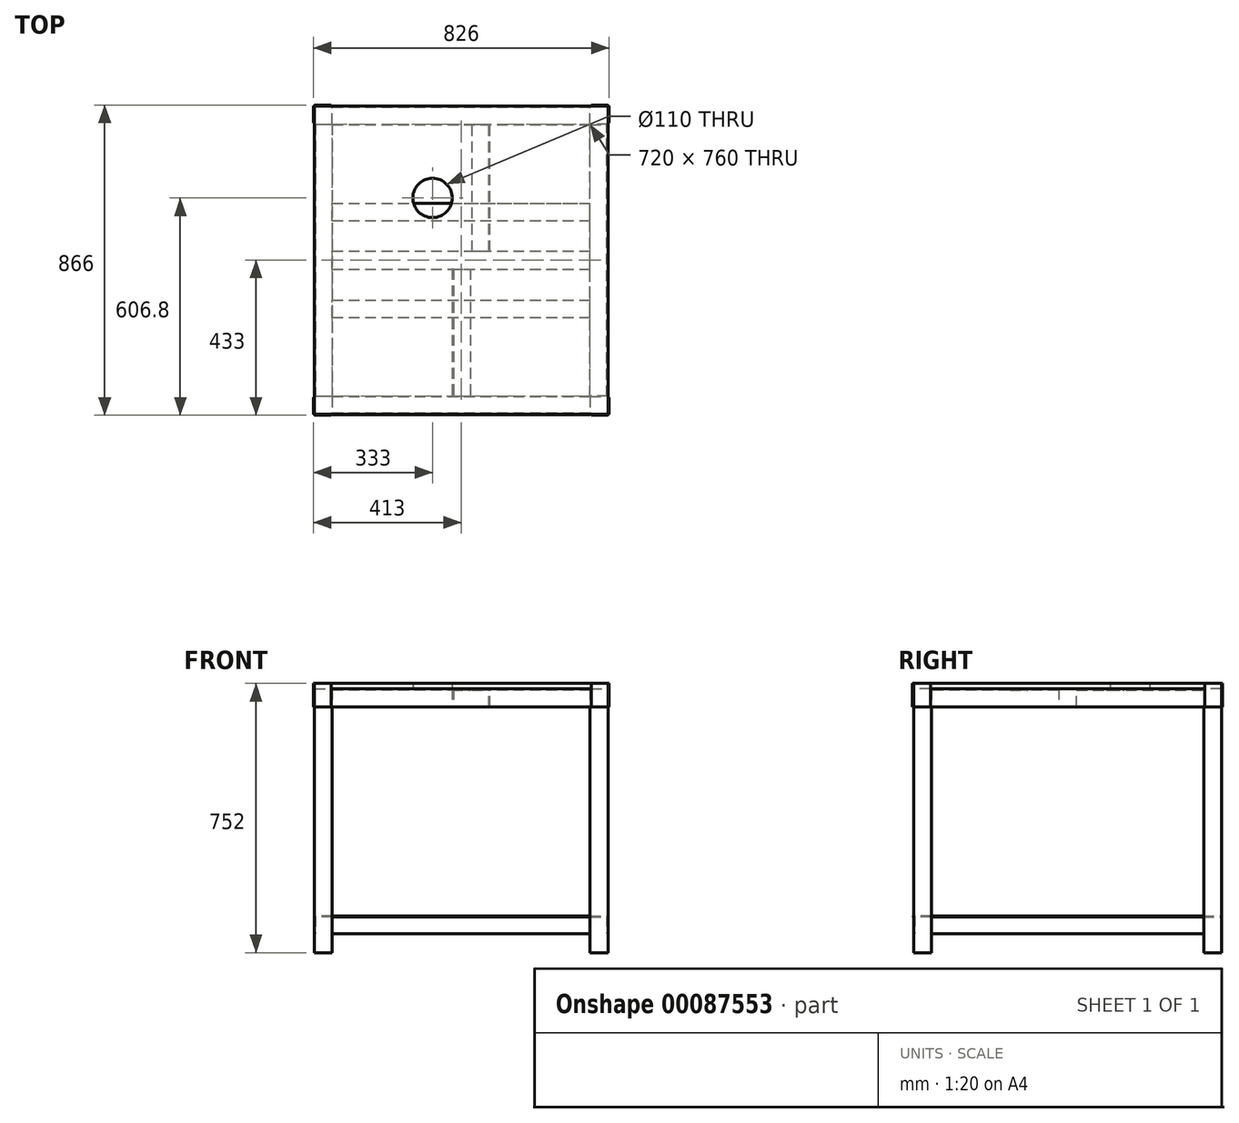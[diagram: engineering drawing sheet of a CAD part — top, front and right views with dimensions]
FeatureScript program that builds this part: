
annotation { "Feature Type Name" : "Feature", "Feature Type Description" : "" }
export const myFeature = defineFeature(function(context is Context, id is Id, definition is map)
    precondition{}
    {
        {
            var Q0;
            Q0=qCreatedBy(makeId("Top.planeOp"),FACE);
            var sketch = newSketch(context, id + "F0", { "sketchPlane" : qUnion([Q0])});
            skLineSegment(sketch, "E0", {"start": v(-475, -20) * mm, "end": v(-475, 410) * mm});
            skLineSegment(sketch, "E1", {"start": v(-475, -20) * mm, "end": v(-475, -450) * mm});
            skLineSegment(sketch, "E2", {"start": v(345, -20) * mm, "end": v(345, -450) * mm});
            skLineSegment(sketch, "E3", {"start": v(345, -20) * mm, "end": v(345, 410) * mm});
            skLineSegment(sketch, "E4", {"start": v(-425, -20) * mm, "end": v(-425, 360) * mm});
            skLineSegment(sketch, "E5", {"start": v(-425, -20) * mm, "end": v(-425, -400) * mm});
            skLineSegment(sketch, "E6", {"start": v(295, -20) * mm, "end": v(295, -400) * mm});
            skLineSegment(sketch, "E7", {"start": v(295, -20) * mm, "end": v(295, 360) * mm});
            skLineSegment(sketch, "E8", {"start": v(-425, 360) * mm, "end": v(295, 360) * mm});
            skLineSegment(sketch, "E9", {"start": v(-475, -450) * mm, "end": v(345, -450) * mm});
            skLineSegment(sketch, "E10", {"start": v(-425, -400) * mm, "end": v(295, -400) * mm});
            skLineSegment(sketch, "E11", {"start": v(-475, 410) * mm, "end": v(345, 410) * mm});
            skSolve(sketch);
        }
        {
            var Q0;
            Q0=makeQuery(id+"F0.imprint","IMPRINT",FACE,{"disambiguationData":[TD([[makeQuery(id+"F0.imprint","IMPRINT",EDGE,{"derivedFrom":sQuery(id+"F0.wireOp",EDGE,"E0")}),-1.0]])]});
            extrude(context, id + "F1", {"entities" : qUnion([Q0]), "depth" : 50 * mm});
        }
        {
            var Q0;
            Q0=makeQuery(id+"F1.opExtrude","SWEPT_BODY",BODY,{"disambiguationData":[OSD([sQuery(id+"F0.wireOp",EDGE,"E0"),sQuery(id+"F0.wireOp",EDGE,"E1"),sQuery(id+"F0.wireOp",EDGE,"E2"),sQuery(id+"F0.wireOp",EDGE,"E3"),sQuery(id+"F0.wireOp",EDGE,"E4"),sQuery(id+"F0.wireOp",EDGE,"E5"),sQuery(id+"F0.wireOp",EDGE,"E6"),sQuery(id+"F0.wireOp",EDGE,"E7"),sQuery(id+"F0.wireOp",EDGE,"E8"),sQuery(id+"F0.wireOp",EDGE,"E9"),sQuery(id+"F0.wireOp",EDGE,"E10"),sQuery(id+"F0.wireOp",EDGE,"E11")])]});
            transform(context, id + "F2", {"entities" : qUnion([Q0]), "transformType" : TransformType.TRANSLATION_3D, "dx" : 65 * mm, "dy" : 20 * mm, "dz" : 0 * mm, "makeCopy" : false});
        }
        {
            var Q0;
            Q0=makeQuery(id+"F1.opExtrude","SWEPT_BODY",BODY,{"disambiguationData":[OSD([sQuery(id+"F0.wireOp",EDGE,"E0"),sQuery(id+"F0.wireOp",EDGE,"E1"),sQuery(id+"F0.wireOp",EDGE,"E2"),sQuery(id+"F0.wireOp",EDGE,"E3"),sQuery(id+"F0.wireOp",EDGE,"E4"),sQuery(id+"F0.wireOp",EDGE,"E5"),sQuery(id+"F0.wireOp",EDGE,"E6"),sQuery(id+"F0.wireOp",EDGE,"E7"),sQuery(id+"F0.wireOp",EDGE,"E8"),sQuery(id+"F0.wireOp",EDGE,"E9"),sQuery(id+"F0.wireOp",EDGE,"E10"),sQuery(id+"F0.wireOp",EDGE,"E11")])]});
            transform(context, id + "F3", {"entities" : qUnion([Q0]), "transformType" : TransformType.TRANSLATION_3D, "dx" : 0 * mm, "dy" : 0 * mm, "dz" : -162 * mm, "makeCopy" : false});
        }
        {
            var Q0;
            Q0=qCreatedBy(makeId("Top.planeOp"),FACE);
            var sketch = newSketch(context, id + "F4", { "sketchPlane" : qUnion([Q0])});
            skLineSegment(sketch, "E12", {"start": v(-450, -20) * mm, "end": v(-450, 410) * mm});
            skLineSegment(sketch, "E13", {"start": v(370, -20) * mm, "end": v(370, -450) * mm});
            skLineSegment(sketch, "E14.bottom", {"start": v(-450, 410) * mm, "end": v(370, 410) * mm});
            skLineSegment(sketch, "E14.top", {"start": v(-450, -450) * mm, "end": v(370, -450) * mm});
            skLineSegment(sketch, "E14.left", {"start": v(-450, 410) * mm, "end": v(-450, -450) * mm});
            skLineSegment(sketch, "E14.right", {"start": v(370, 410) * mm, "end": v(370, -450) * mm});
            skSolve(sketch);
        }
        {
            var Q0;
            {var subQ0=sQuery(id+"F4.wireOp",EDGE,"E14.bottom");Q0=makeQuery(id+"F4.imprint","IMPRINT",FACE,{"disambiguationData":[TD([[makeQuery(id+"F4.imprint","IMPRINT",EDGE,{"derivedFrom":subQ0}),-1.0]])]});}
            extrude(context, id + "F5", {"entities" : qUnion([Q0]), "depth" : 15 * mm});
        }
        {
            var Q0;
            Q0=makeQuery(id+"F5.opExtrude","SWEPT_BODY",BODY,{"disambiguationData":[OSD([sQuery(id+"F4.wireOp",EDGE,"E14.bottom"),sQuery(id+"F4.wireOp",EDGE,"E14.top"),sQuery(id+"F4.wireOp",EDGE,"E14.left"),sQuery(id+"F4.wireOp",EDGE,"E14.right")])]});
            transform(context, id + "F6", {"entities" : qUnion([Q0]), "transformType" : TransformType.TRANSLATION_3D, "dx" : 0 * mm, "dy" : 0 * mm, "dz" : -112 * mm, "makeCopy" : false});
        }
        {
            var Q0;
            Q0=qCreatedBy(makeId("Top.planeOp"),FACE);
            var sketch = newSketch(context, id + "F7", { "sketchPlane" : qUnion([Q0])});
            skLineSegment(sketch, "E15", {"start": v(0, 0) * mm, "end": v(-410, 0) * mm});
            skLineSegment(sketch, "E16", {"start": v(0, 0) * mm, "end": v(410, 0) * mm});
            skLineSegment(sketch, "E17", {"start": v(-410, 0) * mm, "end": v(-410, 380) * mm});
            skLineSegment(sketch, "E18", {"start": v(410, 0) * mm, "end": v(410, 380) * mm});
            skLineSegment(sketch, "E19", {"start": v(-410, 0) * mm, "end": v(-410, -380) * mm});
            skLineSegment(sketch, "E20", {"start": v(410, 0) * mm, "end": v(410, -380) * mm});
            skLineSegment(sketch, "E21.bottom", {"start": v(-410, 380) * mm, "end": v(-360, 380) * mm});
            skLineSegment(sketch, "E21.top", {"start": v(-410, 430) * mm, "end": v(-360, 430) * mm});
            skLineSegment(sketch, "E21.left", {"start": v(-410, 380) * mm, "end": v(-410, 430) * mm});
            skLineSegment(sketch, "E21.right", {"start": v(-360, 380) * mm, "end": v(-360, 430) * mm});
            skLineSegment(sketch, "E22.bottom", {"start": v(-410, -380) * mm, "end": v(-360, -380) * mm});
            skLineSegment(sketch, "E22.top", {"start": v(-410, -430) * mm, "end": v(-360, -430) * mm});
            skLineSegment(sketch, "E22.left", {"start": v(-410, -380) * mm, "end": v(-410, -430) * mm});
            skLineSegment(sketch, "E22.right", {"start": v(-360, -380) * mm, "end": v(-360, -430) * mm});
            skLineSegment(sketch, "E23.bottom", {"start": v(410, -380) * mm, "end": v(360, -380) * mm});
            skLineSegment(sketch, "E23.top", {"start": v(410, -430) * mm, "end": v(360, -430) * mm});
            skLineSegment(sketch, "E23.left", {"start": v(410, -380) * mm, "end": v(410, -430) * mm});
            skLineSegment(sketch, "E23.right", {"start": v(360, -380) * mm, "end": v(360, -430) * mm});
            skLineSegment(sketch, "E24.bottom", {"start": v(410, 380) * mm, "end": v(360, 380) * mm});
            skLineSegment(sketch, "E24.top", {"start": v(410, 430) * mm, "end": v(360, 430) * mm});
            skLineSegment(sketch, "E24.left", {"start": v(410, 380) * mm, "end": v(410, 430) * mm});
            skLineSegment(sketch, "E24.right", {"start": v(360, 380) * mm, "end": v(360, 430) * mm});
            skLineSegment(sketch, "E25", {"start": v(-410, 0) * mm, "end": v(-410, -430) * mm});
            skLineSegment(sketch, "E26", {"start": v(-410, 0) * mm, "end": v(-410, 430) * mm});
            skSolve(sketch);
        }
        {
            var Q0;
            Q0 = qSketchRegion(id + "F7", true);
            extrude(context, id + "F8", {"entities" : qUnion([Q0]), "depth" : 687 * mm});
        }
        {
            var Q0;
            Q0=makeQuery(id+"F8.opExtrude","SWEPT_BODY",BODY,{"disambiguationData":[OSD([sQuery(id+"F7.wireOp",EDGE,"E21.bottom"),sQuery(id+"F7.wireOp",EDGE,"E21.top"),sQuery(id+"F7.wireOp",EDGE,"E21.left"),sQuery(id+"F7.wireOp",EDGE,"E21.right")])]});
            var Q1;
            Q1=makeQuery(id+"F8.opExtrude","SWEPT_BODY",BODY,{"disambiguationData":[OSD([sQuery(id+"F7.wireOp",EDGE,"E22.bottom"),sQuery(id+"F7.wireOp",EDGE,"E22.top"),sQuery(id+"F7.wireOp",EDGE,"E22.left"),sQuery(id+"F7.wireOp",EDGE,"E22.right")])]});
            var Q2;
            Q2=makeQuery(id+"F8.opExtrude","SWEPT_BODY",BODY,{"disambiguationData":[OSD([sQuery(id+"F7.wireOp",EDGE,"E23.bottom"),sQuery(id+"F7.wireOp",EDGE,"E23.top"),sQuery(id+"F7.wireOp",EDGE,"E23.left"),sQuery(id+"F7.wireOp",EDGE,"E23.right")])]});
            var Q3;
            Q3=makeQuery(id+"F8.opExtrude","SWEPT_BODY",BODY,{"disambiguationData":[OSD([sQuery(id+"F7.wireOp",EDGE,"E24.bottom"),sQuery(id+"F7.wireOp",EDGE,"E24.top"),sQuery(id+"F7.wireOp",EDGE,"E24.left"),sQuery(id+"F7.wireOp",EDGE,"E24.right")])]});
            transform(context, id + "F9", {"entities" : qUnion([Q0, Q1, Q2, Q3]), "transformType" : TransformType.TRANSLATION_3D, "dx" : 0 * mm, "dy" : 0 * mm, "dz" : -849 * mm, "makeCopy" : false});
        }
        {
            var Q0;
            Q0=qCreatedBy(makeId("Top.planeOp"),FACE);
            var sketch = newSketch(context, id + "F10", { "sketchPlane" : qUnion([Q0])});
            skLineSegment(sketch, "E27", {"start": v(0, 0) * mm, "end": v(-410, 0) * mm});
            skLineSegment(sketch, "E28", {"start": v(0, 0) * mm, "end": v(410, 0) * mm});
            skLineSegment(sketch, "E29", {"start": v(-410, 0) * mm, "end": v(-410, -383) * mm});
            skLineSegment(sketch, "E30", {"start": v(410, 0) * mm, "end": v(410, -383) * mm});
            skLineSegment(sketch, "E31", {"start": v(-410, 0) * mm, "end": v(-410, 383) * mm});
            skLineSegment(sketch, "E32", {"start": v(410, 0) * mm, "end": v(410, 383) * mm});
            skLineSegment(sketch, "E33.bottom", {"start": v(-410, 383) * mm, "end": v(-413, 383) * mm});
            skLineSegment(sketch, "E33.top", {"start": v(-410, 433) * mm, "end": v(-413, 433) * mm});
            skLineSegment(sketch, "E33.left", {"start": v(-410, 383) * mm, "end": v(-410, 433) * mm});
            skLineSegment(sketch, "E33.right", {"start": v(-413, 383) * mm, "end": v(-413, 433) * mm});
            skLineSegment(sketch, "E34.bottom", {"start": v(-410, -383) * mm, "end": v(-413, -383) * mm});
            skLineSegment(sketch, "E34.top", {"start": v(-410, -433) * mm, "end": v(-413, -433) * mm});
            skLineSegment(sketch, "E34.left", {"start": v(-410, -383) * mm, "end": v(-410, -433) * mm});
            skLineSegment(sketch, "E34.right", {"start": v(-413, -383) * mm, "end": v(-413, -433) * mm});
            skLineSegment(sketch, "E35.bottom", {"start": v(410, -383) * mm, "end": v(413, -383) * mm});
            skLineSegment(sketch, "E35.top", {"start": v(410, -433) * mm, "end": v(413, -433) * mm});
            skLineSegment(sketch, "E35.left", {"start": v(410, -383) * mm, "end": v(410, -433) * mm});
            skLineSegment(sketch, "E35.right", {"start": v(413, -383) * mm, "end": v(413, -433) * mm});
            skLineSegment(sketch, "E36.bottom", {"start": v(410, 383) * mm, "end": v(413, 383) * mm});
            skLineSegment(sketch, "E36.top", {"start": v(410, 433) * mm, "end": v(413, 433) * mm});
            skLineSegment(sketch, "E36.left", {"start": v(410, 383) * mm, "end": v(410, 433) * mm});
            skLineSegment(sketch, "E36.right", {"start": v(413, 383) * mm, "end": v(413, 433) * mm});
            skLineSegment(sketch, "E37.bottom", {"start": v(-413, -433) * mm, "end": v(-363, -433) * mm});
            skLineSegment(sketch, "E37.top", {"start": v(-413, -430) * mm, "end": v(-363, -430) * mm});
            skLineSegment(sketch, "E37.left", {"start": v(-413, -433) * mm, "end": v(-413, -430) * mm});
            skLineSegment(sketch, "E37.right", {"start": v(-363, -433) * mm, "end": v(-363, -430) * mm});
            skLineSegment(sketch, "E38.bottom", {"start": v(413, -433) * mm, "end": v(363, -433) * mm});
            skLineSegment(sketch, "E38.top", {"start": v(413, -430) * mm, "end": v(363, -430) * mm});
            skLineSegment(sketch, "E38.left", {"start": v(413, -433) * mm, "end": v(413, -430) * mm});
            skLineSegment(sketch, "E38.right", {"start": v(363, -433) * mm, "end": v(363, -430) * mm});
            skLineSegment(sketch, "E39.bottom", {"start": v(-413, 433) * mm, "end": v(-363, 433) * mm});
            skLineSegment(sketch, "E39.top", {"start": v(-413, 430) * mm, "end": v(-363, 430) * mm});
            skLineSegment(sketch, "E39.left", {"start": v(-413, 433) * mm, "end": v(-413, 430) * mm});
            skLineSegment(sketch, "E39.right", {"start": v(-363, 433) * mm, "end": v(-363, 430) * mm});
            skLineSegment(sketch, "E40.bottom", {"start": v(413, 433) * mm, "end": v(363, 433) * mm});
            skLineSegment(sketch, "E40.top", {"start": v(413, 430) * mm, "end": v(363, 430) * mm});
            skLineSegment(sketch, "E40.left", {"start": v(413, 433) * mm, "end": v(413, 430) * mm});
            skLineSegment(sketch, "E40.right", {"start": v(363, 433) * mm, "end": v(363, 430) * mm});
            skSolve(sketch);
        }
        {
            var Q0;
            {var subQ0=sQuery(id+"F10.wireOp",EDGE,"E33.bottom");Q0=makeQuery(id+"F10.imprint","IMPRINT",FACE,{"disambiguationData":[TD([[makeQuery(id+"F10.imprint","IMPRINT",EDGE,{"derivedFrom":subQ0}),-1.0]])]});}
            var Q1;
            {var subQ5=sQuery(id+"F10.wireOp",EDGE,"E39.left");Q1=makeQuery(id+"F10.imprint","IMPRINT",FACE,{"disambiguationData":[TD([[makeQuery(id+"F10.imprint","IMPRINT",EDGE,{"derivedFrom":subQ5}),1.0]])]});}
            var Q2;
            {var subQ5=sQuery(id+"F10.wireOp",EDGE,"E39.right");Q2=makeQuery(id+"F10.imprint","IMPRINT",FACE,{"disambiguationData":[TD([[makeQuery(id+"F10.imprint","IMPRINT",EDGE,{"derivedFrom":subQ5}),-1.0]])]});}
            var Q3;
            {var subQ0=sQuery(id+"F10.wireOp",EDGE,"E34.bottom");Q3=makeQuery(id+"F10.imprint","IMPRINT",FACE,{"disambiguationData":[TD([[makeQuery(id+"F10.imprint","IMPRINT",EDGE,{"derivedFrom":subQ0}),1.0]])]});}
            var Q4;
            {var subQ5=sQuery(id+"F10.wireOp",EDGE,"E37.left");Q4=makeQuery(id+"F10.imprint","IMPRINT",FACE,{"disambiguationData":[TD([[makeQuery(id+"F10.imprint","IMPRINT",EDGE,{"derivedFrom":subQ5}),-1.0]])]});}
            var Q5;
            {var subQ5=sQuery(id+"F10.wireOp",EDGE,"E37.right");Q5=makeQuery(id+"F10.imprint","IMPRINT",FACE,{"disambiguationData":[TD([[makeQuery(id+"F10.imprint","IMPRINT",EDGE,{"derivedFrom":subQ5}),1.0]])]});}
            var Q6;
            {var subQ5=sQuery(id+"F10.wireOp",EDGE,"E38.right");Q6=makeQuery(id+"F10.imprint","IMPRINT",FACE,{"disambiguationData":[TD([[makeQuery(id+"F10.imprint","IMPRINT",EDGE,{"derivedFrom":subQ5}),-1.0]])]});}
            var Q7;
            {var subQ5=sQuery(id+"F10.wireOp",EDGE,"E38.left");Q7=makeQuery(id+"F10.imprint","IMPRINT",FACE,{"disambiguationData":[TD([[makeQuery(id+"F10.imprint","IMPRINT",EDGE,{"derivedFrom":subQ5}),1.0]])]});}
            var Q8;
            {var subQ0=sQuery(id+"F10.wireOp",EDGE,"E35.bottom");Q8=makeQuery(id+"F10.imprint","IMPRINT",FACE,{"disambiguationData":[TD([[makeQuery(id+"F10.imprint","IMPRINT",EDGE,{"derivedFrom":subQ0}),-1.0]])]});}
            var Q9;
            {var subQ0=sQuery(id+"F10.wireOp",EDGE,"E36.bottom");Q9=makeQuery(id+"F10.imprint","IMPRINT",FACE,{"disambiguationData":[TD([[makeQuery(id+"F10.imprint","IMPRINT",EDGE,{"derivedFrom":subQ0}),1.0]])]});}
            var Q10;
            {var subQ5=sQuery(id+"F10.wireOp",EDGE,"E40.left");Q10=makeQuery(id+"F10.imprint","IMPRINT",FACE,{"disambiguationData":[TD([[makeQuery(id+"F10.imprint","IMPRINT",EDGE,{"derivedFrom":subQ5}),-1.0]])]});}
            var Q11;
            {var subQ5=sQuery(id+"F10.wireOp",EDGE,"E40.right");Q11=makeQuery(id+"F10.imprint","IMPRINT",FACE,{"disambiguationData":[TD([[makeQuery(id+"F10.imprint","IMPRINT",EDGE,{"derivedFrom":subQ5}),1.0]])]});}
            extrude(context, id + "F11", {"entities" : qUnion([Q0, Q1, Q2, Q3, Q4, Q5, Q6, Q7, Q8, Q9, Q10, Q11]), "depth" : 65 * mm});
        }
        {
            var Q0;
            Q0=makeQuery(id+"F11.opExtrude","SWEPT_BODY",BODY,{"disambiguationData":[OSD([sQuery(id+"F10.wireOp",EDGE,"E33.bottom"),sQuery(id+"F10.wireOp",EDGE,"E33.left"),sQuery(id+"F10.wireOp",EDGE,"E33.right"),sQuery(id+"F10.wireOp",EDGE,"E39.bottom"),sQuery(id+"F10.wireOp",EDGE,"E39.top"),sQuery(id+"F10.wireOp",EDGE,"E39.left"),sQuery(id+"F10.wireOp",EDGE,"E39.right")])]});
            var Q1;
            Q1=makeQuery(id+"F11.opExtrude","SWEPT_BODY",BODY,{"disambiguationData":[OSD([sQuery(id+"F10.wireOp",EDGE,"E34.bottom"),sQuery(id+"F10.wireOp",EDGE,"E34.left"),sQuery(id+"F10.wireOp",EDGE,"E34.right"),sQuery(id+"F10.wireOp",EDGE,"E37.bottom"),sQuery(id+"F10.wireOp",EDGE,"E37.top"),sQuery(id+"F10.wireOp",EDGE,"E37.left"),sQuery(id+"F10.wireOp",EDGE,"E37.right")])]});
            var Q2;
            Q2=makeQuery(id+"F11.opExtrude","SWEPT_BODY",BODY,{"disambiguationData":[OSD([sQuery(id+"F10.wireOp",EDGE,"E35.bottom"),sQuery(id+"F10.wireOp",EDGE,"E35.left"),sQuery(id+"F10.wireOp",EDGE,"E35.right"),sQuery(id+"F10.wireOp",EDGE,"E38.bottom"),sQuery(id+"F10.wireOp",EDGE,"E38.top"),sQuery(id+"F10.wireOp",EDGE,"E38.left"),sQuery(id+"F10.wireOp",EDGE,"E38.right")])]});
            var Q3;
            Q3=makeQuery(id+"F11.opExtrude","SWEPT_BODY",BODY,{"disambiguationData":[OSD([sQuery(id+"F10.wireOp",EDGE,"E36.bottom"),sQuery(id+"F10.wireOp",EDGE,"E36.left"),sQuery(id+"F10.wireOp",EDGE,"E36.right"),sQuery(id+"F10.wireOp",EDGE,"E40.bottom"),sQuery(id+"F10.wireOp",EDGE,"E40.top"),sQuery(id+"F10.wireOp",EDGE,"E40.left"),sQuery(id+"F10.wireOp",EDGE,"E40.right")])]});
            transform(context, id + "F12", {"entities" : qUnion([Q0, Q1, Q2, Q3]), "transformType" : TransformType.TRANSLATION_3D, "dx" : 0 * mm, "dy" : 0 * mm, "dz" : -162 * mm, "makeCopy" : false});
        }
        {
            var Q0;
            Q0=qCreatedBy(makeId("Top.planeOp"),FACE);
            var sketch = newSketch(context, id + "F13", { "sketchPlane" : qUnion([Q0])});
            skLineSegment(sketch, "E41", {"start": v(0, 110) * mm, "end": v(360, 110) * mm});
            skLineSegment(sketch, "E42", {"start": v(0, 110) * mm, "end": v(-360, 110) * mm});
            skLineSegment(sketch, "E43", {"start": v(0, -160) * mm, "end": v(-360, -160) * mm});
            skLineSegment(sketch, "E44", {"start": v(0, -160) * mm, "end": v(360, -160) * mm});
            skLineSegment(sketch, "E45", {"start": v(0, -110) * mm, "end": v(-360, -110) * mm});
            skLineSegment(sketch, "E46", {"start": v(0, -110) * mm, "end": v(360, -110) * mm});
            skLineSegment(sketch, "E47", {"start": v(0, 160) * mm, "end": v(-360, 160) * mm});
            skLineSegment(sketch, "E48", {"start": v(0, 160) * mm, "end": v(360, 160) * mm});
            skLineSegment(sketch, "E49", {"start": v(-360, -160) * mm, "end": v(-360, -110) * mm});
            skLineSegment(sketch, "E50", {"start": v(-360, 110) * mm, "end": v(-360, 160) * mm});
            skLineSegment(sketch, "E51", {"start": v(360, -160) * mm, "end": v(360, -110) * mm});
            skLineSegment(sketch, "E52", {"start": v(360, 110) * mm, "end": v(360, 160) * mm});
            skSolve(sketch);
        }
        {
            var Q0;
            Q0=makeQuery(id+"F13.imprint","IMPRINT",FACE,{"disambiguationData":[TD([[makeQuery(id+"F13.imprint","IMPRINT",EDGE,{"derivedFrom":sQuery(id+"F13.wireOp",EDGE,"E43")}),-1.0]])]});
            var Q1;
            Q1=makeQuery(id+"F13.imprint","IMPRINT",FACE,{"disambiguationData":[TD([[makeQuery(id+"F13.imprint","IMPRINT",EDGE,{"derivedFrom":sQuery(id+"F13.wireOp",EDGE,"E41")}),1.0]])]});
            extrude(context, id + "F14", {"entities" : qUnion([Q0, Q1]), "depth" : 3 * mm});
        }
        {
            var Q0;
            Q0=makeQuery(id+"F14.opExtrude","SWEPT_BODY",BODY,{"disambiguationData":[OSD([sQuery(id+"F13.wireOp",EDGE,"E41"),sQuery(id+"F13.wireOp",EDGE,"E42"),sQuery(id+"F13.wireOp",EDGE,"E47"),sQuery(id+"F13.wireOp",EDGE,"E48"),sQuery(id+"F13.wireOp",EDGE,"E50"),sQuery(id+"F13.wireOp",EDGE,"E52")])]});
            var Q1;
            Q1=makeQuery(id+"F14.opExtrude","SWEPT_BODY",BODY,{"disambiguationData":[OSD([sQuery(id+"F13.wireOp",EDGE,"E43"),sQuery(id+"F13.wireOp",EDGE,"E44"),sQuery(id+"F13.wireOp",EDGE,"E45"),sQuery(id+"F13.wireOp",EDGE,"E46"),sQuery(id+"F13.wireOp",EDGE,"E49"),sQuery(id+"F13.wireOp",EDGE,"E51")])]});
            transform(context, id + "F15", {"entities" : qUnion([Q0, Q1]), "transformType" : TransformType.TRANSLATION_3D, "dx" : 0 * mm, "dy" : 0 * mm, "dz" : -115 * mm, "makeCopy" : false});
        }
        {
            var Q0;
            Q0=qCreatedBy(makeId("Top.planeOp"),FACE);
            var sketch = newSketch(context, id + "F16", { "sketchPlane" : qUnion([Q0])});
            skLineSegment(sketch, "E53", {"start": v(0, 0) * mm, "end": v(0, 157) * mm});
            skLineSegment(sketch, "E54", {"start": v(0, 0) * mm, "end": v(0, -157) * mm});
            skLineSegment(sketch, "E55", {"start": v(0, 157) * mm, "end": v(-360, 157) * mm});
            skLineSegment(sketch, "E56", {"start": v(0, 157) * mm, "end": v(360, 157) * mm});
            skLineSegment(sketch, "E57", {"start": v(0, -157) * mm, "end": v(-360, -157) * mm});
            skLineSegment(sketch, "E58", {"start": v(0, -157) * mm, "end": v(360, -157) * mm});
            skLineSegment(sketch, "E59", {"start": v(-360, 157) * mm, "end": v(-360, 160) * mm});
            skLineSegment(sketch, "E60", {"start": v(360, 157) * mm, "end": v(360, 160) * mm});
            skLineSegment(sketch, "E61", {"start": v(-360, 160) * mm, "end": v(360, 160) * mm});
            skLineSegment(sketch, "E62", {"start": v(-360, -157) * mm, "end": v(-360, -160) * mm});
            skLineSegment(sketch, "E63", {"start": v(360, -157) * mm, "end": v(360, -160) * mm});
            skLineSegment(sketch, "E64", {"start": v(-360, -160) * mm, "end": v(360, -160) * mm});
            skSolve(sketch);
        }
        {
            var Q0;
            Q0=makeQuery(id+"F16.imprint","IMPRINT",FACE,{"disambiguationData":[TD([[makeQuery(id+"F16.imprint","IMPRINT",EDGE,{"derivedFrom":sQuery(id+"F16.wireOp",EDGE,"E55")}),-1.0]])]});
            var Q1;
            Q1=makeQuery(id+"F16.imprint","IMPRINT",FACE,{"disambiguationData":[TD([[makeQuery(id+"F16.imprint","IMPRINT",EDGE,{"derivedFrom":sQuery(id+"F16.wireOp",EDGE,"E57")}),1.0]])]});
            extrude(context, id + "F17", {"entities" : qUnion([Q0, Q1]), "depth" : 50 * mm});
        }
        {
            var Q0;
            Q0=makeQuery(id+"F17.opExtrude","SWEPT_BODY",BODY,{"disambiguationData":[OSD([sQuery(id+"F16.wireOp",EDGE,"E55"),sQuery(id+"F16.wireOp",EDGE,"E56"),sQuery(id+"F16.wireOp",EDGE,"E59"),sQuery(id+"F16.wireOp",EDGE,"E60"),sQuery(id+"F16.wireOp",EDGE,"E61")])]});
            var Q1;
            Q1=makeQuery(id+"F17.opExtrude","SWEPT_BODY",BODY,{"disambiguationData":[OSD([sQuery(id+"F16.wireOp",EDGE,"E57"),sQuery(id+"F16.wireOp",EDGE,"E58"),sQuery(id+"F16.wireOp",EDGE,"E62"),sQuery(id+"F16.wireOp",EDGE,"E63"),sQuery(id+"F16.wireOp",EDGE,"E64")])]});
            transform(context, id + "F18", {"entities" : qUnion([Q0, Q1]), "transformType" : TransformType.TRANSLATION_3D, "dx" : 0 * mm, "dy" : 0 * mm, "dz" : -162 * mm, "makeCopy" : false});
        }
        {
            var Q0;
            Q0=qCreatedBy(makeId("Top.planeOp"),FACE);
            var sketch = newSketch(context, id + "F19", { "sketchPlane" : qUnion([Q0])});
            skLineSegment(sketch, "E65", {"start": v(0, 0) * mm, "end": v(0, -380) * mm});
            skLineSegment(sketch, "E66", {"start": v(0, 0) * mm, "end": v(0, 380) * mm});
            skLineSegment(sketch, "E67", {"start": v(0, 0) * mm, "end": v(-360, 0) * mm});
            skLineSegment(sketch, "E68", {"start": v(0, 0) * mm, "end": v(360, 0) * mm});
            skLineSegment(sketch, "E69", {"start": v(-360, 0) * mm, "end": v(-360, 380) * mm});
            skLineSegment(sketch, "E70", {"start": v(-360, 0) * mm, "end": v(-360, -380) * mm});
            skLineSegment(sketch, "E71", {"start": v(360, 0) * mm, "end": v(360, 380) * mm});
            skLineSegment(sketch, "E72", {"start": v(360, 0) * mm, "end": v(360, -380) * mm});
            skLineSegment(sketch, "E73", {"start": v(-360, -380) * mm, "end": v(-410, -380) * mm});
            skLineSegment(sketch, "E74", {"start": v(-360, 380) * mm, "end": v(-410, 380) * mm});
            skLineSegment(sketch, "E75", {"start": v(360, -380) * mm, "end": v(410, -380) * mm});
            skLineSegment(sketch, "E76", {"start": v(360, 380) * mm, "end": v(410, 380) * mm});
            skLineSegment(sketch, "E77", {"start": v(-410, -380) * mm, "end": v(-410, 380) * mm});
            skLineSegment(sketch, "E78", {"start": v(410, -380) * mm, "end": v(410, 380) * mm});
            skLineSegment(sketch, "E79", {"start": v(-360, -380) * mm, "end": v(-360, -430) * mm});
            skLineSegment(sketch, "E80", {"start": v(360, -380) * mm, "end": v(360, -430) * mm});
            skLineSegment(sketch, "E81", {"start": v(-360, 380) * mm, "end": v(-360, 430) * mm});
            skLineSegment(sketch, "E82", {"start": v(360, 380) * mm, "end": v(360, 430) * mm});
            skLineSegment(sketch, "E83", {"start": v(-360, -430) * mm, "end": v(360, -430) * mm});
            skLineSegment(sketch, "E84", {"start": v(-360, 430) * mm, "end": v(360, 430) * mm});
            skLineSegment(sketch, "E85", {"start": v(-360, 380) * mm, "end": v(360, 380) * mm});
            skLineSegment(sketch, "E86", {"start": v(-360, -380) * mm, "end": v(360, -380) * mm});
            skSolve(sketch);
        }
        {
            var Q0;
            {var subQ2=sQuery(id+"F19.wireOp",EDGE,"E79");Q0=makeQuery(id+"F19.imprint","IMPRINT",FACE,{"disambiguationData":[TD([[makeQuery(id+"F19.imprint","IMPRINT",EDGE,{"derivedFrom":subQ2}),1.0]])]});}
            var Q1;
            Q1=makeQuery(id+"F19.imprint","IMPRINT",FACE,{"disambiguationData":[TD([[makeQuery(id+"F19.imprint","IMPRINT",EDGE,{"derivedFrom":sQuery(id+"F19.wireOp",EDGE,"E69")}),1.0]])]});
            var Q2;
            {var subQ2=sQuery(id+"F19.wireOp",EDGE,"E81");Q2=makeQuery(id+"F19.imprint","IMPRINT",FACE,{"disambiguationData":[TD([[makeQuery(id+"F19.imprint","IMPRINT",EDGE,{"derivedFrom":subQ2}),-1.0]])]});}
            var Q3;
            Q3=makeQuery(id+"F19.imprint","IMPRINT",FACE,{"disambiguationData":[TD([[makeQuery(id+"F19.imprint","IMPRINT",EDGE,{"derivedFrom":sQuery(id+"F19.wireOp",EDGE,"E71")}),-1.0]])]});
            extrude(context, id + "F20", {"entities" : qUnion([Q0, Q1, Q2, Q3]), "depth" : 3 * mm});
        }
        {
            var Q0;
            Q0=makeQuery(id+"F20.opExtrude","SWEPT_BODY",BODY,{"disambiguationData":[OSD([sQuery(id+"F19.wireOp",EDGE,"E69"),sQuery(id+"F19.wireOp",EDGE,"E70"),sQuery(id+"F19.wireOp",EDGE,"E73"),sQuery(id+"F19.wireOp",EDGE,"E74"),sQuery(id+"F19.wireOp",EDGE,"E77")])]});
            var Q1;
            Q1=makeQuery(id+"F20.opExtrude","SWEPT_BODY",BODY,{"disambiguationData":[OSD([sQuery(id+"F19.wireOp",EDGE,"E79"),sQuery(id+"F19.wireOp",EDGE,"E80"),sQuery(id+"F19.wireOp",EDGE,"E83"),sQuery(id+"F19.wireOp",EDGE,"E86")])]});
            var Q2;
            Q2=makeQuery(id+"F20.opExtrude","SWEPT_BODY",BODY,{"disambiguationData":[OSD([sQuery(id+"F19.wireOp",EDGE,"E71"),sQuery(id+"F19.wireOp",EDGE,"E72"),sQuery(id+"F19.wireOp",EDGE,"E75"),sQuery(id+"F19.wireOp",EDGE,"E76"),sQuery(id+"F19.wireOp",EDGE,"E78")])]});
            var Q3;
            Q3=makeQuery(id+"F20.opExtrude","SWEPT_BODY",BODY,{"disambiguationData":[OSD([sQuery(id+"F19.wireOp",EDGE,"E81"),sQuery(id+"F19.wireOp",EDGE,"E82"),sQuery(id+"F19.wireOp",EDGE,"E84"),sQuery(id+"F19.wireOp",EDGE,"E85")])]});
            transform(context, id + "F21", {"entities" : qUnion([Q0, Q1, Q2, Q3]), "transformType" : TransformType.TRANSLATION_3D, "dx" : 0 * mm, "dy" : 0 * mm, "dz" : -749 * mm, "makeCopy" : false});
        }
        {
            var Q0;
            Q0=qCreatedBy(makeId("Top.planeOp"),FACE);
            var sketch = newSketch(context, id + "F22", { "sketchPlane" : qUnion([Q0])});
            skLineSegment(sketch, "E87", {"start": v(0, 0) * mm, "end": v(0, -427) * mm});
            skLineSegment(sketch, "E88", {"start": v(0, 0) * mm, "end": v(0, 427) * mm});
            skLineSegment(sketch, "E89", {"start": v(0, 0) * mm, "end": v(-407, 0) * mm});
            skLineSegment(sketch, "E90", {"start": v(0, 0) * mm, "end": v(407, 0) * mm});
            skLineSegment(sketch, "E91", {"start": v(0, 427) * mm, "end": v(-360, 427) * mm});
            skLineSegment(sketch, "E92", {"start": v(0, 427) * mm, "end": v(360, 427) * mm});
            skLineSegment(sketch, "E93", {"start": v(0, -427) * mm, "end": v(-360, -427) * mm});
            skLineSegment(sketch, "E94", {"start": v(0, -427) * mm, "end": v(360, -427) * mm});
            skLineSegment(sketch, "E95", {"start": v(-407, 0) * mm, "end": v(-407, -380) * mm});
            skLineSegment(sketch, "E96", {"start": v(-407, 0) * mm, "end": v(-407, 380) * mm});
            skLineSegment(sketch, "E97", {"start": v(407, 0) * mm, "end": v(407, 380) * mm});
            skLineSegment(sketch, "E98", {"start": v(407, 0) * mm, "end": v(407, -380) * mm});
            skLineSegment(sketch, "E99", {"start": v(-360, -427) * mm, "end": v(-360, -430) * mm});
            skLineSegment(sketch, "E100", {"start": v(-407, -380) * mm, "end": v(-410, -380) * mm});
            skLineSegment(sketch, "E101", {"start": v(360, -427) * mm, "end": v(360, -430) * mm});
            skLineSegment(sketch, "E102", {"start": v(407, -380) * mm, "end": v(410, -380) * mm});
            skLineSegment(sketch, "E103", {"start": v(407, 380) * mm, "end": v(410, 380) * mm});
            skLineSegment(sketch, "E104", {"start": v(360, 427) * mm, "end": v(360, 430) * mm});
            skLineSegment(sketch, "E105", {"start": v(-407, 380) * mm, "end": v(-410, 380) * mm});
            skLineSegment(sketch, "E106", {"start": v(-360, 427) * mm, "end": v(-360, 430) * mm});
            skLineSegment(sketch, "E107", {"start": v(-410, -380) * mm, "end": v(-410, 380) * mm});
            skLineSegment(sketch, "E108", {"start": v(-360, 430) * mm, "end": v(360, 430) * mm});
            skLineSegment(sketch, "E109", {"start": v(410, 380) * mm, "end": v(410, -380) * mm});
            skLineSegment(sketch, "E110", {"start": v(360, -430) * mm, "end": v(-360, -430) * mm});
            skSolve(sketch);
        }
        {
            var Q0;
            Q0=makeQuery(id+"F22.imprint","IMPRINT",FACE,{"disambiguationData":[TD([[makeQuery(id+"F22.imprint","IMPRINT",EDGE,{"derivedFrom":sQuery(id+"F22.wireOp",EDGE,"E93")}),1.0]])]});
            var Q1;
            Q1=makeQuery(id+"F22.imprint","IMPRINT",FACE,{"disambiguationData":[TD([[makeQuery(id+"F22.imprint","IMPRINT",EDGE,{"derivedFrom":sQuery(id+"F22.wireOp",EDGE,"E97")}),-1.0]])]});
            var Q2;
            Q2=makeQuery(id+"F22.imprint","IMPRINT",FACE,{"disambiguationData":[TD([[makeQuery(id+"F22.imprint","IMPRINT",EDGE,{"derivedFrom":sQuery(id+"F22.wireOp",EDGE,"E95")}),-1.0]])]});
            var Q3;
            Q3=makeQuery(id+"F22.imprint","IMPRINT",FACE,{"disambiguationData":[TD([[makeQuery(id+"F22.imprint","IMPRINT",EDGE,{"derivedFrom":sQuery(id+"F22.wireOp",EDGE,"E91")}),-1.0]])]});
            extrude(context, id + "F23", {"entities" : qUnion([Q0, Q1, Q2, Q3]), "depth" : 50 * mm});
        }
        {
            var Q0;
            Q0=makeQuery(id+"F23.opExtrude","SWEPT_BODY",BODY,{"disambiguationData":[OSD([sQuery(id+"F22.wireOp",EDGE,"E95"),sQuery(id+"F22.wireOp",EDGE,"E96"),sQuery(id+"F22.wireOp",EDGE,"E100"),sQuery(id+"F22.wireOp",EDGE,"E105"),sQuery(id+"F22.wireOp",EDGE,"E107")])]});
            var Q1;
            Q1=makeQuery(id+"F23.opExtrude","SWEPT_BODY",BODY,{"disambiguationData":[OSD([sQuery(id+"F22.wireOp",EDGE,"E93"),sQuery(id+"F22.wireOp",EDGE,"E94"),sQuery(id+"F22.wireOp",EDGE,"E99"),sQuery(id+"F22.wireOp",EDGE,"E101"),sQuery(id+"F22.wireOp",EDGE,"E110")])]});
            var Q2;
            Q2=makeQuery(id+"F23.opExtrude","SWEPT_BODY",BODY,{"disambiguationData":[OSD([sQuery(id+"F22.wireOp",EDGE,"E97"),sQuery(id+"F22.wireOp",EDGE,"E98"),sQuery(id+"F22.wireOp",EDGE,"E102"),sQuery(id+"F22.wireOp",EDGE,"E103"),sQuery(id+"F22.wireOp",EDGE,"E109")])]});
            var Q3;
            Q3=makeQuery(id+"F23.opExtrude","SWEPT_BODY",BODY,{"disambiguationData":[OSD([sQuery(id+"F22.wireOp",EDGE,"E91"),sQuery(id+"F22.wireOp",EDGE,"E92"),sQuery(id+"F22.wireOp",EDGE,"E104"),sQuery(id+"F22.wireOp",EDGE,"E106"),sQuery(id+"F22.wireOp",EDGE,"E108")])]});
            transform(context, id + "F24", {"entities" : qUnion([Q0, Q1, Q2, Q3]), "transformType" : TransformType.TRANSLATION_3D, "dx" : 0 * mm, "dy" : 0 * mm, "dz" : -796 * mm, "makeCopy" : false});
        }
        {
            var Q0;
            Q0=makeQuery(id+"F5.opExtrude","SWEPT_BODY",BODY,{"disambiguationData":[OSD([sQuery(id+"F4.wireOp",EDGE,"E14.bottom"),sQuery(id+"F4.wireOp",EDGE,"E14.top"),sQuery(id+"F4.wireOp",EDGE,"E14.left"),sQuery(id+"F4.wireOp",EDGE,"E14.right")])]});
            transform(context, id + "F25", {"entities" : qUnion([Q0]), "transformType" : TransformType.TRANSLATION_3D, "dx" : 40 * mm, "dy" : 20 * mm, "dz" : 0 * mm, "makeCopy" : false});
        }
        {
            var Q0;
            Q0=makeQuery(id+"F1.opExtrude","SWEPT_BODY",BODY,{"disambiguationData":[OSD([sQuery(id+"F0.wireOp",EDGE,"E0"),sQuery(id+"F0.wireOp",EDGE,"E1"),sQuery(id+"F0.wireOp",EDGE,"E2"),sQuery(id+"F0.wireOp",EDGE,"E3"),sQuery(id+"F0.wireOp",EDGE,"E4"),sQuery(id+"F0.wireOp",EDGE,"E5"),sQuery(id+"F0.wireOp",EDGE,"E6"),sQuery(id+"F0.wireOp",EDGE,"E7"),sQuery(id+"F0.wireOp",EDGE,"E8"),sQuery(id+"F0.wireOp",EDGE,"E9"),sQuery(id+"F0.wireOp",EDGE,"E10"),sQuery(id+"F0.wireOp",EDGE,"E11")])]});
            var Q1;
            Q1=makeQuery(id+"F5.opExtrude","SWEPT_BODY",BODY,{"disambiguationData":[OSD([sQuery(id+"F4.wireOp",EDGE,"E14.bottom"),sQuery(id+"F4.wireOp",EDGE,"E14.top"),sQuery(id+"F4.wireOp",EDGE,"E14.left"),sQuery(id+"F4.wireOp",EDGE,"E14.right")])]});
            var Q2;
            Q2=makeQuery(id+"F8.opExtrude","SWEPT_BODY",BODY,{"disambiguationData":[OSD([sQuery(id+"F7.wireOp",EDGE,"E22.bottom"),sQuery(id+"F7.wireOp",EDGE,"E22.top"),sQuery(id+"F7.wireOp",EDGE,"E22.right"),sQuery(id+"F7.wireOp",EDGE,"E25")])]});
            var Q3;
            Q3=makeQuery(id+"F8.opExtrude","SWEPT_BODY",BODY,{"disambiguationData":[OSD([sQuery(id+"F7.wireOp",EDGE,"E23.bottom"),sQuery(id+"F7.wireOp",EDGE,"E23.top"),sQuery(id+"F7.wireOp",EDGE,"E23.left"),sQuery(id+"F7.wireOp",EDGE,"E23.right")])]});
            var Q4;
            Q4=makeQuery(id+"F8.opExtrude","SWEPT_BODY",BODY,{"disambiguationData":[OSD([sQuery(id+"F7.wireOp",EDGE,"E24.bottom"),sQuery(id+"F7.wireOp",EDGE,"E24.top"),sQuery(id+"F7.wireOp",EDGE,"E24.left"),sQuery(id+"F7.wireOp",EDGE,"E24.right")])]});
            var Q5;
            Q5=makeQuery(id+"F11.opExtrude","SWEPT_BODY",BODY,{"disambiguationData":[OSD([sQuery(id+"F10.wireOp",EDGE,"E33.bottom"),sQuery(id+"F10.wireOp",EDGE,"E33.left"),sQuery(id+"F10.wireOp",EDGE,"E33.right"),sQuery(id+"F10.wireOp",EDGE,"E39.bottom"),sQuery(id+"F10.wireOp",EDGE,"E39.top"),sQuery(id+"F10.wireOp",EDGE,"E39.left"),sQuery(id+"F10.wireOp",EDGE,"E39.right")])]});
            var Q6;
            Q6=makeQuery(id+"F11.opExtrude","SWEPT_BODY",BODY,{"disambiguationData":[OSD([sQuery(id+"F10.wireOp",EDGE,"E34.bottom"),sQuery(id+"F10.wireOp",EDGE,"E34.left"),sQuery(id+"F10.wireOp",EDGE,"E34.right"),sQuery(id+"F10.wireOp",EDGE,"E37.bottom"),sQuery(id+"F10.wireOp",EDGE,"E37.top"),sQuery(id+"F10.wireOp",EDGE,"E37.left"),sQuery(id+"F10.wireOp",EDGE,"E37.right")])]});
            var Q7;
            Q7=makeQuery(id+"F11.opExtrude","SWEPT_BODY",BODY,{"disambiguationData":[OSD([sQuery(id+"F10.wireOp",EDGE,"E35.bottom"),sQuery(id+"F10.wireOp",EDGE,"E35.left"),sQuery(id+"F10.wireOp",EDGE,"E35.right"),sQuery(id+"F10.wireOp",EDGE,"E38.bottom"),sQuery(id+"F10.wireOp",EDGE,"E38.top"),sQuery(id+"F10.wireOp",EDGE,"E38.left"),sQuery(id+"F10.wireOp",EDGE,"E38.right")])]});
            var Q8;
            Q8=makeQuery(id+"F11.opExtrude","SWEPT_BODY",BODY,{"disambiguationData":[OSD([sQuery(id+"F10.wireOp",EDGE,"E36.bottom"),sQuery(id+"F10.wireOp",EDGE,"E36.left"),sQuery(id+"F10.wireOp",EDGE,"E36.right"),sQuery(id+"F10.wireOp",EDGE,"E40.bottom"),sQuery(id+"F10.wireOp",EDGE,"E40.top"),sQuery(id+"F10.wireOp",EDGE,"E40.left"),sQuery(id+"F10.wireOp",EDGE,"E40.right")])]});
            var Q9;
            Q9=makeQuery(id+"F23.opExtrude","SWEPT_BODY",BODY,{"disambiguationData":[OSD([sQuery(id+"F22.wireOp",EDGE,"E91"),sQuery(id+"F22.wireOp",EDGE,"E92"),sQuery(id+"F22.wireOp",EDGE,"E104"),sQuery(id+"F22.wireOp",EDGE,"E106"),sQuery(id+"F22.wireOp",EDGE,"E108")])]});
            var Q10;
            Q10=makeQuery(id+"F23.opExtrude","SWEPT_BODY",BODY,{"disambiguationData":[OSD([sQuery(id+"F22.wireOp",EDGE,"E93"),sQuery(id+"F22.wireOp",EDGE,"E94"),sQuery(id+"F22.wireOp",EDGE,"E99"),sQuery(id+"F22.wireOp",EDGE,"E101"),sQuery(id+"F22.wireOp",EDGE,"E110")])]});
            var Q11;
            Q11=makeQuery(id+"F23.opExtrude","SWEPT_BODY",BODY,{"disambiguationData":[OSD([sQuery(id+"F22.wireOp",EDGE,"E95"),sQuery(id+"F22.wireOp",EDGE,"E96"),sQuery(id+"F22.wireOp",EDGE,"E100"),sQuery(id+"F22.wireOp",EDGE,"E105"),sQuery(id+"F22.wireOp",EDGE,"E107")])]});
            var Q12;
            Q12=makeQuery(id+"F23.opExtrude","SWEPT_BODY",BODY,{"disambiguationData":[OSD([sQuery(id+"F22.wireOp",EDGE,"E97"),sQuery(id+"F22.wireOp",EDGE,"E98"),sQuery(id+"F22.wireOp",EDGE,"E102"),sQuery(id+"F22.wireOp",EDGE,"E103"),sQuery(id+"F22.wireOp",EDGE,"E109")])]});
            var Q13;
            Q13=makeQuery(id+"F8.opExtrude","SWEPT_BODY",BODY,{"disambiguationData":[OSD([sQuery(id+"F7.wireOp",EDGE,"E21.bottom"),sQuery(id+"F7.wireOp",EDGE,"E21.top"),sQuery(id+"F7.wireOp",EDGE,"E21.right"),sQuery(id+"F7.wireOp",EDGE,"E26")])]});
            var Q14;
            Q14=makeQuery(id+"F17.opExtrude","SWEPT_BODY",BODY,{"disambiguationData":[OSD([sQuery(id+"F16.wireOp",EDGE,"E55"),sQuery(id+"F16.wireOp",EDGE,"E56"),sQuery(id+"F16.wireOp",EDGE,"E59"),sQuery(id+"F16.wireOp",EDGE,"E60"),sQuery(id+"F16.wireOp",EDGE,"E61")])]});
            var Q15;
            Q15=makeQuery(id+"F17.opExtrude","SWEPT_BODY",BODY,{"disambiguationData":[OSD([sQuery(id+"F16.wireOp",EDGE,"E57"),sQuery(id+"F16.wireOp",EDGE,"E58"),sQuery(id+"F16.wireOp",EDGE,"E62"),sQuery(id+"F16.wireOp",EDGE,"E63"),sQuery(id+"F16.wireOp",EDGE,"E64")])]});
            transform(context, id + "F26", {"entities" : qUnion([Q0, Q1, Q2, Q3, Q4, Q5, Q6, Q7, Q8, Q9, Q10, Q11, Q12, Q13, Q14, Q15]), "transformType" : TransformType.TRANSLATION_3D, "dx" : 0 * mm, "dy" : 1.2 * mm, "dz" : 0 * mm, "makeCopy" : false});
        }
        {
            var Q0;
            Q0=qCreatedBy(makeId("Top.planeOp"),FACE);
            var sketch = newSketch(context, id + "F27", { "sketchPlane" : qUnion([Q0])});
            skLineSegment(sketch, "E111", {"start": v(0, 0) * mm, "end": v(0, -428.8) * mm});
            skLineSegment(sketch, "E112", {"start": v(0, 120) * mm, "end": v(0, -428.8) * mm});
            skLineSegment(sketch, "E113", {"start": v(0, 120) * mm, "end": v(-25, 120) * mm});
            skLineSegment(sketch, "E114", {"start": v(0, 120) * mm, "end": v(0, 175) * mm});
            skLineSegment(sketch, "E115", {"start": v(-25, 120) * mm, "end": v(-80, 120) * mm});
            skLineSegment(sketch, "E116", {"start": v(-80, 120) * mm, "end": v(-80, 175) * mm});
            skCircle(sketch, "E117", {"center": v(-80, 175) * mm, "radius": 55 * mm});
            skSolve(sketch);
        }
        {
            var Q0;
            Q0=makeQuery(id+"F27.imprint","IMPRINT",FACE,{"disambiguationData":[TD([[makeQuery(id+"F27.imprint","IMPRINT",EDGE,{"derivedFrom":sQuery(id+"F27.wireOp",EDGE,"E117")}),1.0]])]});
            extrude(context, id + "F28", {"entities" : qUnion([Q0]), "depth" : 25 * mm});
        }
        {
            var Q0;
            Q0=makeQuery(id+"F28.opExtrude","SWEPT_BODY",BODY,{"disambiguationData":[OSD([sQuery(id+"F27.wireOp",EDGE,"E117")])]});
            transform(context, id + "F29", {"entities" : qUnion([Q0]), "transformType" : TransformType.TRANSLATION_3D, "dx" : 0 * mm, "dy" : 0 * mm, "dz" : -120 * mm, "makeCopy" : false});
        }
        {
            var Q0;
            Q0=makeQuery(id+"F28.opExtrude","SWEPT_BODY",BODY,{"disambiguationData":[OSD([sQuery(id+"F27.wireOp",EDGE,"E117")])]});
            var Q1;
            Q1=makeQuery(id+"F5.opExtrude","SWEPT_BODY",BODY,{"disambiguationData":[OSD([sQuery(id+"F4.wireOp",EDGE,"E14.bottom"),sQuery(id+"F4.wireOp",EDGE,"E14.top"),sQuery(id+"F4.wireOp",EDGE,"E14.left"),sQuery(id+"F4.wireOp",EDGE,"E14.right")])]});
            booleanBodies(context, id + "F30", {"operationType" : BooleanOperationType.SUBTRACTION, "tools" : qUnion([Q0]), "targets" : qUnion([Q1])});
        }
        {
            var Q0;
            Q0=qCreatedBy(makeId("Top.planeOp"),FACE);
            var sketch = newSketch(context, id + "F31", { "sketchPlane" : qUnion([Q0])});
            skCircle(sketch, "E118", {"center": v(0, 0) * mm, "radius": 110 * mm});
            skSolve(sketch);
        }
        {
            var Q0;
            Q0=makeQuery(id+"F31.imprint","IMPRINT",FACE,{"disambiguationData":[TD([[makeQuery(id+"F31.imprint","IMPRINT",EDGE,{"derivedFrom":sQuery(id+"F31.wireOp",EDGE,"E118")}),1.0]])]});
            extrude(context, id + "F32", {"entities" : qUnion([Q0]), "depth" : 100 * mm});
        }
        {
            var Q0;
            Q0=makeQuery(id+"F32.opExtrude","SWEPT_BODY",BODY,{"disambiguationData":[OSD([sQuery(id+"F31.wireOp",EDGE,"E118")])]});
            transform(context, id + "F33", {"entities" : qUnion([Q0]), "transformType" : TransformType.TRANSLATION_3D, "dx" : -80 * mm, "dy" : 175 * mm, "dz" : -150 * mm, "makeCopy" : false});
        }
        {
            var Q0;
            Q0=makeQuery(id+"F17.opExtrude","SWEPT_BODY",BODY,{"disambiguationData":[OSD([sQuery(id+"F16.wireOp",EDGE,"E57"),sQuery(id+"F16.wireOp",EDGE,"E58"),sQuery(id+"F16.wireOp",EDGE,"E62"),sQuery(id+"F16.wireOp",EDGE,"E63"),sQuery(id+"F16.wireOp",EDGE,"E64")])]});
            transform(context, id + "F34", {"entities" : qUnion([Q0]), "transformType" : TransformType.TRANSLATION_3D, "dx" : 0 * mm, "dy" : 135 * mm, "dz" : 0 * mm, "makeCopy" : false});
        }
        {
            var Q0;
            Q0=qCreatedBy(makeId("Top.planeOp"),FACE);
            var sketch = newSketch(context, id + "F35", { "sketchPlane" : qUnion([Q0])});
            skLineSegment(sketch, "E119", {"start": v(0, 0) * mm, "end": v(0, -25) * mm});
            skLineSegment(sketch, "E120", {"start": v(-360, -25) * mm, "end": v(-360, 25) * mm});
            skLineSegment(sketch, "E121", {"start": v(360, -25) * mm, "end": v(360, 25) * mm});
            skLineSegment(sketch, "E122", {"start": v(-360, 25) * mm, "end": v(30, 25) * mm});
            skLineSegment(sketch, "E123", {"start": v(-360, -25) * mm, "end": v(30, -25) * mm});
            skLineSegment(sketch, "E124", {"start": v(30, -25) * mm, "end": v(360, -25) * mm});
            skLineSegment(sketch, "E125", {"start": v(30, 25) * mm, "end": v(98.81, 25) * mm});
            skLineSegment(sketch, "E126", {"start": v(98.81, 25) * mm, "end": v(360, 25) * mm});
            skSolve(sketch);
        }
        {
            var Q0;
            {var subQ2=sQuery(id+"F35.wireOp",EDGE,"E120");Q0=makeQuery(id+"F35.imprint","IMPRINT",FACE,{"disambiguationData":[TD([[makeQuery(id+"F35.imprint","IMPRINT",EDGE,{"derivedFrom":subQ2}),-1.0]])]});}
            extrude(context, id + "F36", {"entities" : qUnion([Q0]), "depth" : 50 * mm});
        }
        {
            var Q0;
            Q0=makeQuery(id+"F36.opExtrude","SWEPT_BODY",BODY,{"disambiguationData":[OSD([sQuery(id+"F35.wireOp",EDGE,"E120"),sQuery(id+"F35.wireOp",EDGE,"E121"),sQuery(id+"F35.wireOp",EDGE,"E122"),sQuery(id+"F35.wireOp",EDGE,"E123"),sQuery(id+"F35.wireOp",EDGE,"E124"),sQuery(id+"F35.wireOp",EDGE,"E125"),sQuery(id+"F35.wireOp",EDGE,"E126")])]});
            transform(context, id + "F37", {"entities" : qUnion([Q0]), "transformType" : TransformType.TRANSLATION_3D, "dx" : 0 * mm, "dy" : 1.2 * mm, "dz" : -162 * mm, "makeCopy" : false});
        }
        {
            var Q0;
            Q0=qCreatedBy(makeId("Top.planeOp"),FACE);
            var sketch = newSketch(context, id + "F38", { "sketchPlane" : qUnion([Q0])});
            skLineSegment(sketch, "E127", {"start": v(0, 0) * mm, "end": v(30, 0) * mm});
            skLineSegment(sketch, "E128", {"start": v(30, 0) * mm, "end": v(30, 25) * mm});
            skLineSegment(sketch, "E129", {"start": v(30, 25) * mm, "end": v(30, 380) * mm});
            skLineSegment(sketch, "E130", {"start": v(80, 25) * mm, "end": v(80, 380) * mm});
            skLineSegment(sketch, "E131", {"start": v(30, 380) * mm, "end": v(80, 380) * mm});
            skLineSegment(sketch, "E132", {"start": v(30, 25) * mm, "end": v(80, 25) * mm});
            skLineSegment(sketch, "E133", {"start": v(0, 0) * mm, "end": v(0, -25) * mm});
            skLineSegment(sketch, "E134", {"start": v(0, -25) * mm, "end": v(-25, -25) * mm});
            skLineSegment(sketch, "E135", {"start": v(0, -25) * mm, "end": v(25, -25) * mm});
            skLineSegment(sketch, "E136", {"start": v(-25, -25) * mm, "end": v(-25, -380) * mm});
            skLineSegment(sketch, "E137", {"start": v(25, -25) * mm, "end": v(25, -380) * mm});
            skLineSegment(sketch, "E138", {"start": v(-25, -380) * mm, "end": v(25, -380) * mm});
            skSolve(sketch);
        }
        {
            var Q0;
            Q0=makeQuery(id+"F38.imprint","IMPRINT",FACE,{"disambiguationData":[TD([[makeQuery(id+"F38.imprint","IMPRINT",EDGE,{"derivedFrom":sQuery(id+"F38.wireOp",EDGE,"E129")}),-1.0]])]});
            var Q1;
            Q1=makeQuery(id+"F38.imprint","IMPRINT",FACE,{"disambiguationData":[TD([[makeQuery(id+"F38.imprint","IMPRINT",EDGE,{"derivedFrom":sQuery(id+"F38.wireOp",EDGE,"E134")}),1.0]])]});
            extrude(context, id + "F39", {"entities" : qUnion([Q0, Q1]), "depth" : 3 * mm});
        }
        {
            var Q0;
            Q0=makeQuery(id+"F39.opExtrude","SWEPT_BODY",BODY,{"disambiguationData":[OSD([sQuery(id+"F38.wireOp",EDGE,"E129"),sQuery(id+"F38.wireOp",EDGE,"E130"),sQuery(id+"F38.wireOp",EDGE,"E131"),sQuery(id+"F38.wireOp",EDGE,"E132")])]});
            var Q1;
            Q1=makeQuery(id+"F39.opExtrude","SWEPT_BODY",BODY,{"disambiguationData":[OSD([sQuery(id+"F38.wireOp",EDGE,"E134"),sQuery(id+"F38.wireOp",EDGE,"E135"),sQuery(id+"F38.wireOp",EDGE,"E136"),sQuery(id+"F38.wireOp",EDGE,"E137"),sQuery(id+"F38.wireOp",EDGE,"E138")])]});
            transform(context, id + "F40", {"entities" : qUnion([Q0, Q1]), "transformType" : TransformType.TRANSLATION_3D, "dx" : 0 * mm, "dy" : 1.2 * mm, "dz" : -115 * mm, "makeCopy" : false});
        }
        {
            var Q0;
            Q0=makeQuery(id+"F17.opExtrude","SWEPT_BODY",BODY,{"disambiguationData":[OSD([sQuery(id+"F16.wireOp",EDGE,"E55"),sQuery(id+"F16.wireOp",EDGE,"E56"),sQuery(id+"F16.wireOp",EDGE,"E59"),sQuery(id+"F16.wireOp",EDGE,"E60"),sQuery(id+"F16.wireOp",EDGE,"E61")])]});
            deleteBodies(context, id + "F41", {"entities" : qUnion([Q0])});
        }
        {
            var Q0;
            Q0=makeQuery(id+"F17.opExtrude","SWEPT_BODY",BODY,{"disambiguationData":[OSD([sQuery(id+"F16.wireOp",EDGE,"E57"),sQuery(id+"F16.wireOp",EDGE,"E58"),sQuery(id+"F16.wireOp",EDGE,"E62"),sQuery(id+"F16.wireOp",EDGE,"E63"),sQuery(id+"F16.wireOp",EDGE,"E64")])]});
            deleteBodies(context, id + "F42", {"entities" : qUnion([Q0])});
        }
        {
            var Q0;
            Q0=makeQuery(id+"F39.opExtrude","SWEPT_BODY",BODY,{"disambiguationData":[OSD([sQuery(id+"F38.wireOp",EDGE,"E129"),sQuery(id+"F38.wireOp",EDGE,"E130"),sQuery(id+"F38.wireOp",EDGE,"E131"),sQuery(id+"F38.wireOp",EDGE,"E132")])]});
            var Q1;
            Q1=makeQuery(id+"F39.opExtrude","CAP_EDGE",EDGE,{"disambiguationData":[OSD([sQuery(id+"F38.wireOp",EDGE,"E130")])],"isStart":false});
            transform(context, id + "F43", {"entities" : qUnion([Q0]), "transformType" : TransformType.ROTATION, "transformAxis" : qUnion([Q1]), "angle" : 270 * degree, "makeCopy" : true});
        }
        {
            var Q0;
            Q0=makeQuery(id+"F43.opPattern","COPY",BODY,{"derivedFrom":makeQuery(id+"F39.opExtrude","SWEPT_BODY",BODY,{"disambiguationData":[OSD([sQuery(id+"F38.wireOp",EDGE,"E129"),sQuery(id+"F38.wireOp",EDGE,"E130"),sQuery(id+"F38.wireOp",EDGE,"E131"),sQuery(id+"F38.wireOp",EDGE,"E132")])]}),"instanceName":"1"});
            transform(context, id + "F44", {"entities" : qUnion([Q0]), "transformType" : TransformType.TRANSLATION_3D, "dx" : -3 * mm, "dy" : 0 * mm, "dz" : 0 * mm, "makeCopy" : false});
        }
        {
            var Q0;
            Q0=makeQuery(id+"F39.opExtrude","SWEPT_BODY",BODY,{"disambiguationData":[OSD([sQuery(id+"F38.wireOp",EDGE,"E134"),sQuery(id+"F38.wireOp",EDGE,"E135"),sQuery(id+"F38.wireOp",EDGE,"E136"),sQuery(id+"F38.wireOp",EDGE,"E137"),sQuery(id+"F38.wireOp",EDGE,"E138")])]});
            var Q1;
            Q1=makeQuery(id+"F39.opExtrude","CAP_EDGE",EDGE,{"disambiguationData":[OSD([sQuery(id+"F38.wireOp",EDGE,"E136")])],"isStart":false});
            transform(context, id + "F45", {"entities" : qUnion([Q0]), "transformType" : TransformType.ROTATION, "transformAxis" : qUnion([Q1]), "angle" : 270 * degree, "makeCopy" : true});
        }
        {
            var Q0;
            Q0=makeQuery(id+"F45.opPattern","COPY",BODY,{"derivedFrom":makeQuery(id+"F39.opExtrude","SWEPT_BODY",BODY,{"disambiguationData":[OSD([sQuery(id+"F38.wireOp",EDGE,"E134"),sQuery(id+"F38.wireOp",EDGE,"E135"),sQuery(id+"F38.wireOp",EDGE,"E136"),sQuery(id+"F38.wireOp",EDGE,"E137"),sQuery(id+"F38.wireOp",EDGE,"E138")])]}),"instanceName":"1"});
            transform(context, id + "F46", {"entities" : qUnion([Q0]), "transformType" : TransformType.TRANSLATION_3D, "dx" : 3 * mm, "dy" : 0 * mm, "dz" : 0 * mm, "makeCopy" : false});
        }
        {
            var Q0;
            Q0=makeQuery(id+"F32.opExtrude","SWEPT_BODY",BODY,{"disambiguationData":[OSD([sQuery(id+"F31.wireOp",EDGE,"E118")])]});
            deleteBodies(context, id + "F47", {"entities" : qUnion([Q0])});
        }
    });
